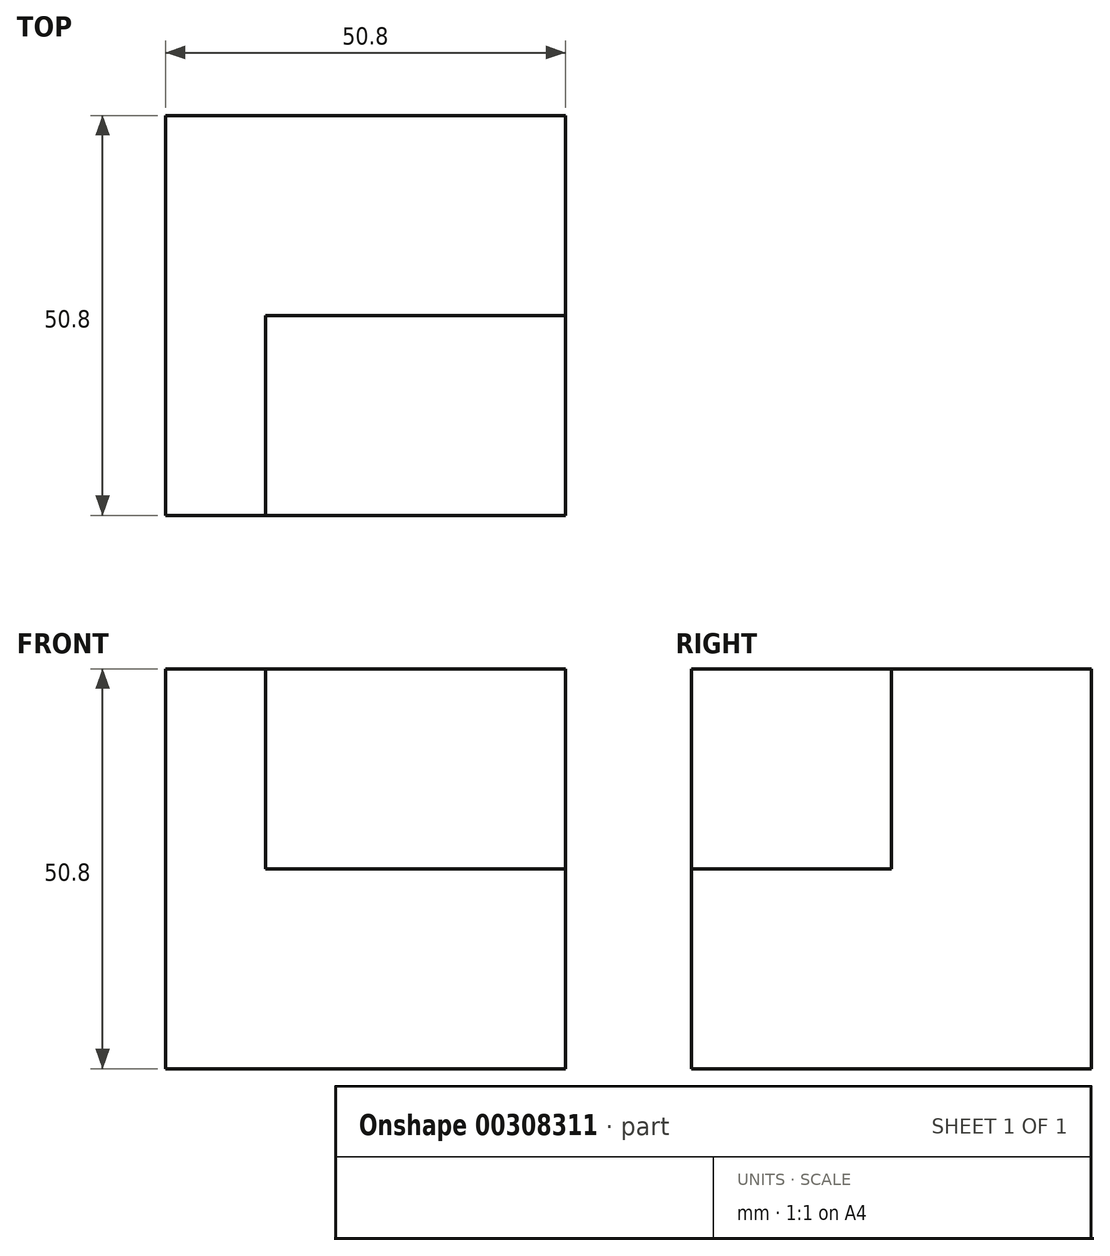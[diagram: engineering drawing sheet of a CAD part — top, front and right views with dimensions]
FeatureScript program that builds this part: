
annotation { "Feature Type Name" : "Feature", "Feature Type Description" : "" }
export const myFeature = defineFeature(function(context is Context, id is Id, definition is map)
    precondition{}
    {
        {
            var Q0;
            Q0=qCreatedBy(makeId("Right.planeOp"),FACE);
            var sketch = newSketch(context, id + "F0", { "sketchPlane" : qUnion([Q0])});
            skLineSegment(sketch, "E0", {"start": v(-27.24, -31.2) * mm, "end": v(23.56, -31.2) * mm});
            skLineSegment(sketch, "E1", {"start": v(23.56, -31.2) * mm, "end": v(23.56, 19.6) * mm});
            skLineSegment(sketch, "E2", {"start": v(-27.24, -31.2) * mm, "end": v(-27.24, 19.6) * mm});
            skLineSegment(sketch, "E3", {"start": v(-27.24, 19.6) * mm, "end": v(23.56, 19.6) * mm});
            skSolve(sketch);
        }
        {
            var Q0;
            Q0=makeQuery(id+"F0.imprint","IMPRINT",FACE,{"disambiguationData":[TD([[makeQuery(id+"F0.imprint","IMPRINT",EDGE,{"derivedFrom":sQuery(id+"F0.wireOp",EDGE,"E0")}),1.0]])]});
            extrude(context, id + "F1", {"entities" : qUnion([Q0]), "oppositeDirection" : true, "depth" : 50.8 * mm});
        }
        {
            var Q0;
            Q0=makeQuery(id+"F1.opExtrude","CAP_FACE",FACE,{"disambiguationData":[OSD([sQuery(id+"F0.wireOp",EDGE,"E0"),sQuery(id+"F0.wireOp",EDGE,"E1"),sQuery(id+"F0.wireOp",EDGE,"E2"),sQuery(id+"F0.wireOp",EDGE,"E3")])],"isStart":true});
            var sketch = newSketch(context, id + "F2", { "sketchPlane" : qUnion([Q0])});
            skLineSegment(sketch, "E4.bottom", {"start": v(-27.24, 19.6) * mm, "end": v(-1.84, 19.6) * mm});
            skLineSegment(sketch, "E4.top", {"start": v(-27.24, -5.8) * mm, "end": v(-1.84, -5.8) * mm});
            skLineSegment(sketch, "E4.left", {"start": v(-27.24, 19.6) * mm, "end": v(-27.24, -5.8) * mm});
            skLineSegment(sketch, "E4.right", {"start": v(-1.84, 19.6) * mm, "end": v(-1.84, -5.8) * mm});
            skLineSegment(sketch, "E5", {"start": v(-1.84, 19.6) * mm, "end": v(23.56, 19.6) * mm});
            skSolve(sketch);
        }
        {
            var Q0;
            Q0=makeQuery(id+"F2.imprint","IMPRINT",FACE,{"disambiguationData":[TD([[makeQuery(id+"F2.imprint","IMPRINT",EDGE,{"derivedFrom":sQuery(id+"F2.wireOp",EDGE,"E4.bottom")}),-1.0]])]});
            extrude(context, id + "F3", {"entities" : qUnion([Q0]), "operationType" : NewBodyOperationType.REMOVE, "oppositeDirection" : true, "depth" : 38.1 * mm});
        }
    });
